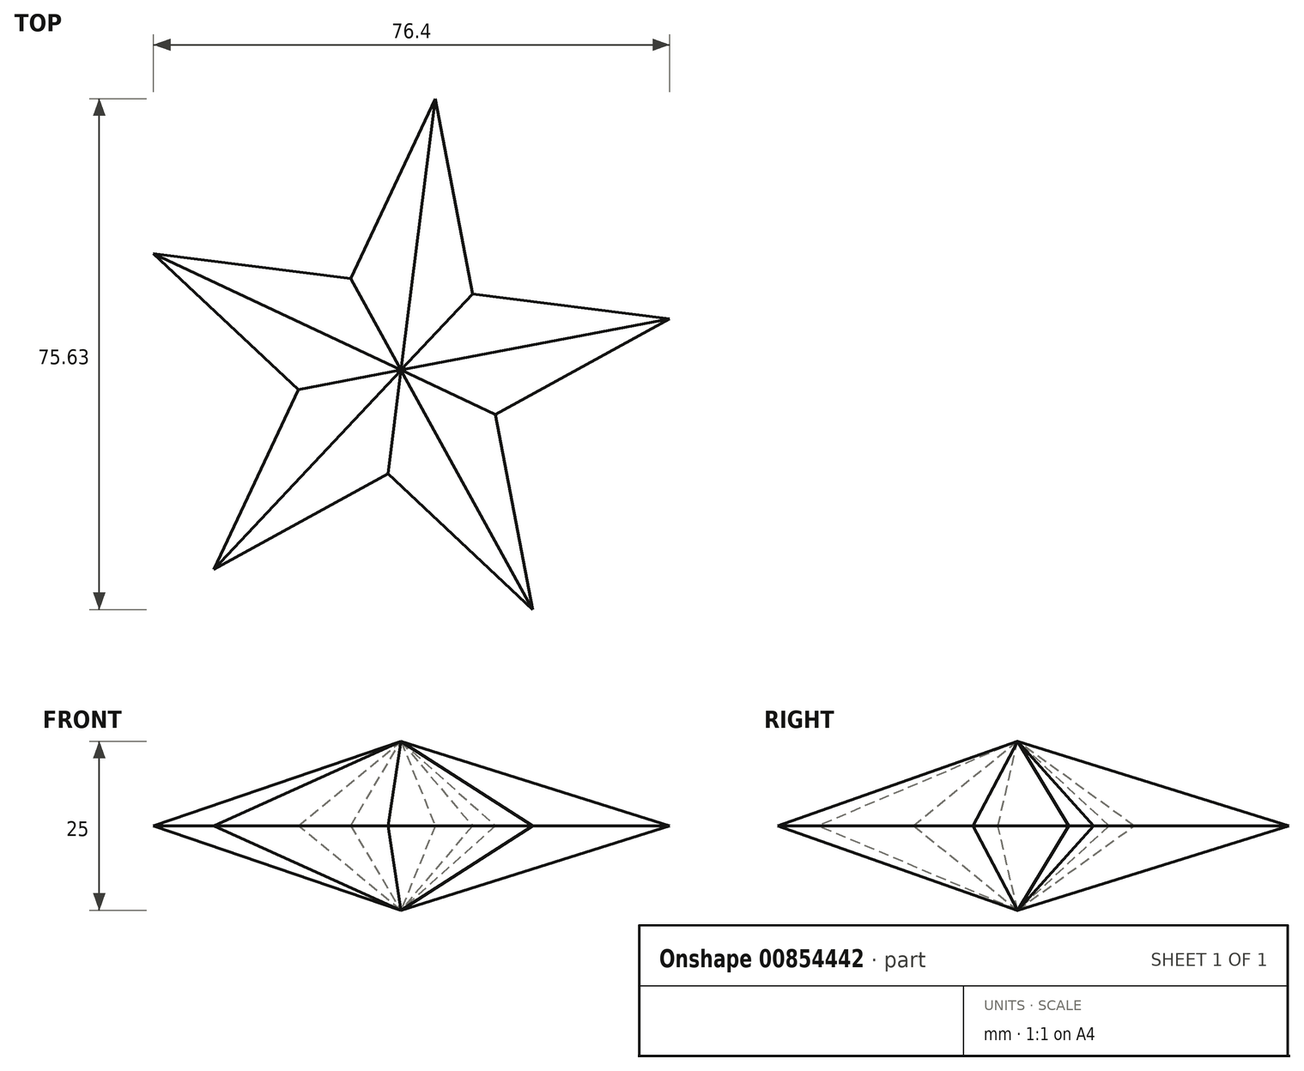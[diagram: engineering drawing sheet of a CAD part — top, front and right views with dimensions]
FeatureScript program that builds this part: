
annotation { "Feature Type Name" : "Feature", "Feature Type Description" : "" }
export const myFeature = defineFeature(function(context is Context, id is Id, definition is map)
    precondition{}
    {
        {
            var Q0;
            Q0=qCreatedBy(makeId("Top.planeOp"),FACE);
            var sketch = newSketch(context, id + "F0", { "sketchPlane" : qUnion([Q0])});
            skPoint(sketch, "E0.0.midPoint", {"position": v(40.7, 43.34) * mm});
            skLineSegment(sketch, "E1", {"start": v(-50.3, -53.58) * mm, "end": v(72.19, 13.78) * mm});
            skLineSegment(sketch, "E2", {"start": v(72.19, 13.78) * mm, "end": v(-66.5, 31.29) * mm});
            skLineSegment(sketch, "E3", {"start": v(-66.5, 31.29) * mm, "end": v(35.4, -64.4) * mm});
            skLineSegment(sketch, "E4", {"start": v(35.4, -64.4) * mm, "end": v(9.2, 72.91) * mm});
            skLineSegment(sketch, "E5", {"start": v(9.2, 72.91) * mm, "end": v(-50.3, -53.58) * mm});
            skSolve(sketch);
        }
        {
            var Q0;
            Q0 = qSketchRegion(id + "F0", true);
            extrude(context, id + "F1", {"entities" : qUnion([Q0]), "depth" : 25 * mm, "offsetDistance" : 25 * mm});
        }
        {
            var Q0;
            Q0=makeQuery(id+"F1.opExtrude","CAP_FACE",FACE,{"disambiguationData":[OSD([sQuery(id+"F0.wireOp",EDGE,"E1"),sQuery(id+"F0.wireOp",EDGE,"E2"),sQuery(id+"F0.wireOp",EDGE,"E3"),sQuery(id+"F0.wireOp",EDGE,"E4"),sQuery(id+"F0.wireOp",EDGE,"E5")])],"isStart":false});
            chamfer(context, id + "F2", {"entities" : qUnion([Q0]), "width" : 22.7 * mm, "tangentPropagation" : true});
        }
        {
            var Q0;
            Q0=makeQuery(id+"F1.opExtrude","CAP_FACE",FACE,{"disambiguationData":[OSD([sQuery(id+"F0.wireOp",EDGE,"E1"),sQuery(id+"F0.wireOp",EDGE,"E2"),sQuery(id+"F0.wireOp",EDGE,"E3"),sQuery(id+"F0.wireOp",EDGE,"E4"),sQuery(id+"F0.wireOp",EDGE,"E5")])],"isStart":true});
            chamfer(context, id + "F3", {"entities" : qUnion([Q0]), "width" : 22.7 * mm, "tangentPropagation" : true});
        }
    });
